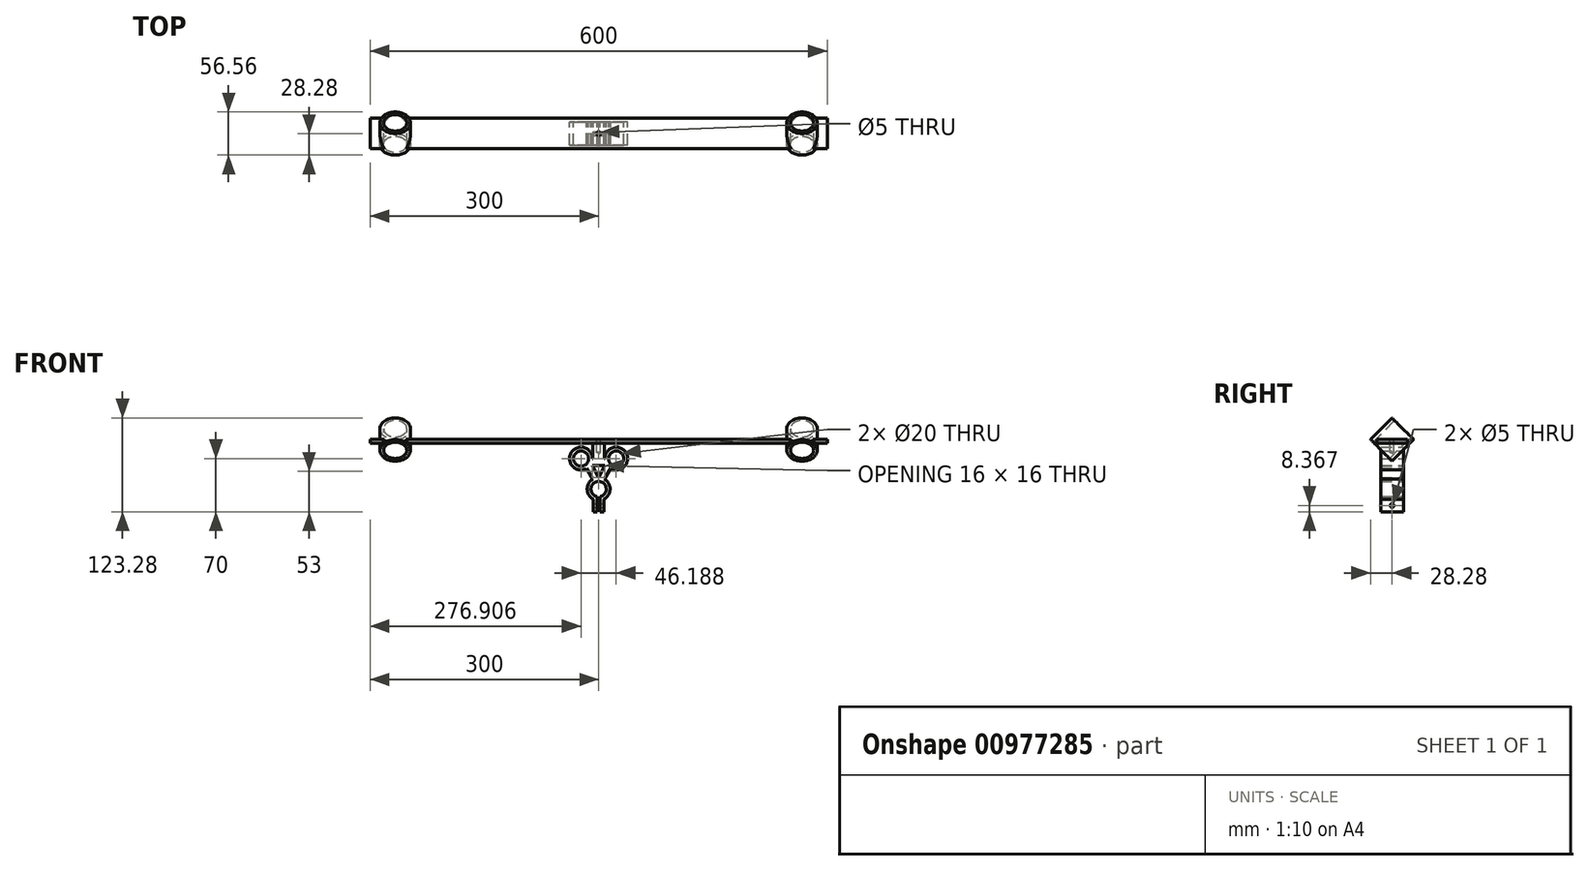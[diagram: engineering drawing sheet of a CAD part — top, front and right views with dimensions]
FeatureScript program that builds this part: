
annotation { "Feature Type Name" : "Feature", "Feature Type Description" : "" }
export const myFeature = defineFeature(function(context is Context, id is Id, definition is map)
    precondition{}
    {
        {
            var Q0;
            Q0=qCreatedBy(makeId("Front.planeOp"),FACE);
            var sketch = newSketch(context, id + "F0", { "sketchPlane" : qUnion([Q0])});
            skCircle(sketch, "E0", {"center": v(0, 0) * mm, "radius": 10 * mm});
            skCircle(sketch, "E1", {"center": v(23.1, 40) * mm, "radius": 10 * mm});
            skCircle(sketch, "E2", {"center": v(-23.1, 40) * mm, "radius": 10 * mm});
            skCircle(sketch, "E3", {"center": v(-23.1, 40) * mm, "radius": 15 * mm});
            skCircle(sketch, "E4", {"center": v(23.1, 40) * mm, "radius": 15 * mm});
            skCircle(sketch, "E5", {"center": v(0, 0) * mm, "radius": 15 * mm});
            skLineSegment(sketch, "E6", {"start": v(0, 0) * mm, "end": v(-23.1, 40) * mm});
            skLineSegment(sketch, "E7", {"start": v(23.1, 40) * mm, "end": v(0, 0) * mm});
            skLineSegment(sketch, "E8", {"start": v(-23.1, 40) * mm, "end": v(23.1, 40) * mm});
            skLineSegment(sketch, "E9.bottom", {"start": v(-2, 0) * mm, "end": v(2, 0) * mm});
            skLineSegment(sketch, "E9.top", {"start": v(-2, -30) * mm, "end": v(2, -30) * mm});
            skLineSegment(sketch, "E9.left", {"start": v(-2, 0) * mm, "end": v(-2, -30) * mm});
            skLineSegment(sketch, "E9.right", {"start": v(2, 0) * mm, "end": v(2, -30) * mm});
            skPoint(sketch, "E9.middle", {"position": v(0, -15) * mm});
            skLineSegment(sketch, "E10.bottom", {"start": v(7, -30) * mm, "end": v(-7, -30) * mm});
            skLineSegment(sketch, "E10.top", {"start": v(7, 0) * mm, "end": v(-7, 0) * mm});
            skLineSegment(sketch, "E10.left", {"start": v(7, -30) * mm, "end": v(7, 0) * mm});
            skLineSegment(sketch, "E10.right", {"start": v(-7, -30) * mm, "end": v(-7, 0) * mm});
            skLineSegment(sketch, "E11.bottom", {"start": v(-7.5, 60) * mm, "end": v(7.5, 60) * mm});
            skLineSegment(sketch, "E11.top", {"start": v(-7.5, 20) * mm, "end": v(7.5, 20) * mm});
            skLineSegment(sketch, "E11.left", {"start": v(-7.5, 60) * mm, "end": v(-7.5, 20) * mm});
            skLineSegment(sketch, "E11.right", {"start": v(7.5, 60) * mm, "end": v(7.5, 20) * mm});
            skPoint(sketch, "E11.middle", {"position": v(0, 40) * mm});
            skSolve(sketch);
        }
        {
            var Q0;
            {var subQ0=sQuery(id+"F0.wireOp",EDGE,"E7");var subQ1=sQuery(id+"F0.wireOp",EDGE,"E1");var subQ2=makeQuery(id+"F0.imprint","INTERSECT",VERTEX,{"derivedFrom":[subQ1,subQ0]});Q0=makeQuery(id+"F0.imprint","IMPRINT",FACE,{"disambiguationData":[TD([[makeQuery(id+"F0.imprint","IMPRINT",EDGE,{"disambiguationData":[TD([[subQ2,-1.0]])],"derivedFrom":subQ1}),-1.0]])]});}
            var Q1;
            {var subQ0=sQuery(id+"F0.wireOp",EDGE,"E6");var subQ1=sQuery(id+"F0.wireOp",EDGE,"E2");var subQ2=makeQuery(id+"F0.imprint","INTERSECT",VERTEX,{"derivedFrom":[subQ1,subQ0]});Q1=makeQuery(id+"F0.imprint","IMPRINT",FACE,{"disambiguationData":[TD([[makeQuery(id+"F0.imprint","IMPRINT",EDGE,{"disambiguationData":[TD([[subQ2,1.0]])],"derivedFrom":subQ1}),-1.0]])]});}
            var Q2;
            {var subQ0=sQuery(id+"F0.wireOp",EDGE,"E10.right");var subQ1=sQuery(id+"F0.wireOp",EDGE,"E5");var subQ2=makeQuery(id+"F0.imprint","INTERSECT",VERTEX,{"derivedFrom":[subQ1,subQ0]});Q2=makeQuery(id+"F0.imprint","IMPRINT",FACE,{"disambiguationData":[TD([[makeQuery(id+"F0.imprint","IMPRINT",EDGE,{"disambiguationData":[TD([[subQ2,-1.0]])],"derivedFrom":subQ1}),-1.0]])]});}
            var Q3;
            {var subQ0=sQuery(id+"F0.wireOp",EDGE,"E10.left");var subQ1=sQuery(id+"F0.wireOp",EDGE,"E5");var subQ2=makeQuery(id+"F0.imprint","INTERSECT",VERTEX,{"derivedFrom":[subQ1,subQ0]});Q3=makeQuery(id+"F0.imprint","IMPRINT",FACE,{"disambiguationData":[TD([[makeQuery(id+"F0.imprint","IMPRINT",EDGE,{"disambiguationData":[TD([[subQ2,1.0]])],"derivedFrom":subQ1}),-1.0]])]});}
            var Q4;
            {var subQ0=sQuery(id+"F0.wireOp",EDGE,"E6");var subQ1=sQuery(id+"F0.wireOp",EDGE,"E0");var subQ2=makeQuery(id+"F0.imprint","INTERSECT",VERTEX,{"derivedFrom":[subQ1,subQ0]});Q4=makeQuery(id+"F0.imprint","IMPRINT",FACE,{"disambiguationData":[TD([[makeQuery(id+"F0.imprint","IMPRINT",EDGE,{"disambiguationData":[TD([[subQ2,-1.0]])],"derivedFrom":subQ1}),-1.0]])]});}
            var Q5;
            {var subQ0=sQuery(id+"F0.wireOp",EDGE,"E7");var subQ1=sQuery(id+"F0.wireOp",EDGE,"E0");var subQ2=makeQuery(id+"F0.imprint","INTERSECT",VERTEX,{"derivedFrom":[subQ1,subQ0]});Q5=makeQuery(id+"F0.imprint","IMPRINT",FACE,{"disambiguationData":[TD([[makeQuery(id+"F0.imprint","IMPRINT",EDGE,{"disambiguationData":[TD([[subQ2,1.0]])],"derivedFrom":subQ1}),-1.0]])]});}
            var Q6;
            {var subQ0=sQuery(id+"F0.wireOp",EDGE,"E7");var subQ1=sQuery(id+"F0.wireOp",EDGE,"E1");var subQ2=makeQuery(id+"F0.imprint","INTERSECT",VERTEX,{"derivedFrom":[subQ1,subQ0]});Q6=makeQuery(id+"F0.imprint","IMPRINT",FACE,{"disambiguationData":[TD([[makeQuery(id+"F0.imprint","IMPRINT",EDGE,{"disambiguationData":[TD([[subQ2,1.0]])],"derivedFrom":subQ1}),-1.0]])]});}
            var Q7;
            {var subQ0=sQuery(id+"F0.wireOp",EDGE,"E6");var subQ1=sQuery(id+"F0.wireOp",EDGE,"E2");var subQ2=makeQuery(id+"F0.imprint","INTERSECT",VERTEX,{"derivedFrom":[subQ1,subQ0]});Q7=makeQuery(id+"F0.imprint","IMPRINT",FACE,{"disambiguationData":[TD([[makeQuery(id+"F0.imprint","IMPRINT",EDGE,{"disambiguationData":[TD([[subQ2,-1.0]])],"derivedFrom":subQ1}),-1.0]])]});}
            var Q8;
            {var subQ0=sQuery(id+"F0.wireOp",EDGE,"E6");var subQ5=sQuery(id+"F0.wireOp",EDGE,"E3");var subQ6=makeQuery(id+"F0.imprint","INTERSECT",VERTEX,{"derivedFrom":[subQ5,subQ0]});Q8=makeQuery(id+"F0.imprint","IMPRINT",FACE,{"disambiguationData":[TD([[makeQuery(id+"F0.imprint","IMPRINT",EDGE,{"disambiguationData":[TD([[subQ6,-1.0]])],"derivedFrom":subQ5}),-1.0]])]});}
            var Q9;
            {var subQ0=sQuery(id+"F0.wireOp",EDGE,"E6");var subQ1=sQuery(id+"F0.wireOp",EDGE,"E0");var subQ2=makeQuery(id+"F0.imprint","INTERSECT",VERTEX,{"derivedFrom":[subQ1,subQ0]});Q9=makeQuery(id+"F0.imprint","IMPRINT",FACE,{"disambiguationData":[TD([[makeQuery(id+"F0.imprint","IMPRINT",EDGE,{"disambiguationData":[TD([[subQ2,1.0]])],"derivedFrom":subQ1}),-1.0]])]});}
            var Q10;
            {var subQ0=sQuery(id+"F0.wireOp",EDGE,"E10.right");var subQ1=sQuery(id+"F0.wireOp",EDGE,"E0");var subQ2=makeQuery(id+"F0.imprint","INTERSECT",VERTEX,{"derivedFrom":[subQ1,subQ0]});Q10=makeQuery(id+"F0.imprint","IMPRINT",FACE,{"disambiguationData":[TD([[makeQuery(id+"F0.imprint","IMPRINT",EDGE,{"disambiguationData":[TD([[subQ2,-1.0]])],"derivedFrom":subQ1}),-1.0]])]});}
            var Q11;
            {var subQ0=sQuery(id+"F0.wireOp",EDGE,"E9.right");var subQ1=sQuery(id+"F0.wireOp",EDGE,"E0");var subQ2=makeQuery(id+"F0.imprint","INTERSECT",VERTEX,{"derivedFrom":[subQ1,subQ0]});Q11=makeQuery(id+"F0.imprint","IMPRINT",FACE,{"disambiguationData":[TD([[makeQuery(id+"F0.imprint","IMPRINT",EDGE,{"disambiguationData":[TD([[subQ2,-1.0]])],"derivedFrom":subQ1}),-1.0]])]});}
            var Q12;
            {var subQ5=sQuery(id+"F0.wireOp",EDGE,"E11.top");Q12=makeQuery(id+"F0.imprint","IMPRINT",FACE,{"disambiguationData":[TD([[makeQuery(id+"F0.imprint","IMPRINT",EDGE,{"derivedFrom":subQ5}),1.0]])]});}
            var Q13;
            {var subQ5=sQuery(id+"F0.wireOp",EDGE,"E11.bottom");Q13=makeQuery(id+"F0.imprint","IMPRINT",FACE,{"disambiguationData":[TD([[makeQuery(id+"F0.imprint","IMPRINT",EDGE,{"derivedFrom":subQ5}),-1.0]])]});}
            extrude(context, id + "F1", {"entities" : qUnion([Q0, Q1, Q2, Q3, Q4, Q5, Q6, Q7, Q8, Q9, Q10, Q11, Q12, Q13]), "depth" : 30 * mm, "offsetDistance" : 25 * mm});
        }
        {
            var Q0;
            Q0=makeQuery(id+"F1.opExtrude","SWEPT_FACE",FACE,{"disambiguationData":[OSD([sQuery(id+"F0.wireOp",EDGE,"E11.bottom")])]});
            var sketch = newSketch(context, id + "F2", { "sketchPlane" : qUnion([Q0])});
            skPoint(sketch, "E12", {"position": v(0, -15) * mm});
            skPoint(sketch, "E12.positionSnap0", {"position": v(-7.5, -15) * mm});
            skSolve(sketch);
        }
        {
            var Q0;
            Q0=sQuery(id+"F2.wireOp",VERTEX,"E12");
            var Q1;
            Q1=makeQuery(id+"F1.opExtrude","SWEPT_BODY",BODY,{"disambiguationData":[OSD([sQuery(id+"F0.wireOp",EDGE,"E0"),sQuery(id+"F0.wireOp",EDGE,"E1"),sQuery(id+"F0.wireOp",EDGE,"E2"),sQuery(id+"F0.wireOp",EDGE,"E3"),sQuery(id+"F0.wireOp",EDGE,"E4"),sQuery(id+"F0.wireOp",EDGE,"E5"),sQuery(id+"F0.wireOp",EDGE,"E6"),sQuery(id+"F0.wireOp",EDGE,"E7"),sQuery(id+"F0.wireOp",EDGE,"E8"),sQuery(id+"F0.wireOp",EDGE,"E9.left"),sQuery(id+"F0.wireOp",EDGE,"E9.right"),sQuery(id+"F0.wireOp",EDGE,"E10.bottom"),sQuery(id+"F0.wireOp",EDGE,"E10.left"),sQuery(id+"F0.wireOp",EDGE,"E10.right"),sQuery(id+"F0.wireOp",EDGE,"E11.bottom"),sQuery(id+"F0.wireOp",EDGE,"E11.left"),sQuery(id+"F0.wireOp",EDGE,"E11.right")])]});
            hole(context, id + "F3", {"style" : HoleStyle.SIMPLE, "endStyle" : HoleEndStyle.BLIND, "holeDiameter" : 5 * mm, "majorDiameter" : 5 * mm, "holeDepth" : 12 * mm, "isTappedThrough" : true, "tappedDepth" : 12 * mm, "tapClearance" : 3, "locations" : qUnion([Q0]), "scope" : qUnion([Q1])});
        }
        {
            var Q0;
            Q0=makeQuery(id+"F1.opExtrude","SWEPT_FACE",FACE,{"disambiguationData":[OSD([sQuery(id+"F0.wireOp",EDGE,"E10.left")])]});
            var sketch = newSketch(context, id + "F4", { "sketchPlane" : qUnion([Q0])});
            skPoint(sketch, "E13", {"position": v(-15, -21.63) * mm});
            skPoint(sketch, "E13.positionSnap0", {"position": v(0, -21.63) * mm});
            skPoint(sketch, "E13.positionSnap1", {"position": v(-15, -30) * mm});
            skCircle(sketch, "E14", {"center": v(-15, -21.63) * mm, "radius": 2.5 * mm});
            skSolve(sketch);
        }
        {
            var Q0;
            Q0=makeQuery(id+"F4.imprint","IMPRINT",FACE,{"disambiguationData":[TD([[makeQuery(id+"F4.imprint","IMPRINT",EDGE,{"derivedFrom":sQuery(id+"F4.wireOp",EDGE,"E14")}),1.0]])]});
            extrude(context, id + "F5", {"entities" : qUnion([Q0]), "operationType" : NewBodyOperationType.REMOVE, "oppositeDirection" : true, "depth" : 25 * mm, "offsetDistance" : 25 * mm});
        }
        {
            var Q0;
            Q0=makeQuery(id+"F1.opExtrude","SWEPT_FACE",FACE,{"disambiguationData":[OSD([sQuery(id+"F0.wireOp",EDGE,"E11.bottom")])]});
            var sketch = newSketch(context, id + "F6", { "sketchPlane" : qUnion([Q0])});
            skLineSegment(sketch, "E15.bottom", {"start": v(-300, 5) * mm, "end": v(300, 5) * mm});
            skLineSegment(sketch, "E15.top", {"start": v(-300, -35) * mm, "end": v(300, -35) * mm});
            skLineSegment(sketch, "E15.left", {"start": v(-300, 5) * mm, "end": v(-300, -35) * mm});
            skLineSegment(sketch, "E15.right", {"start": v(300, 5) * mm, "end": v(300, -35) * mm});
            skPoint(sketch, "E15.middle", {"position": v(0, -15) * mm});
            skSolve(sketch);
        }
        {
            var Q0;
            Q0=qSketchRegion(id+"F6",true);
            extrude(context, id + "F7", {"entities" : qUnion([Q0]), "operationType" : NewBodyOperationType.ADD, "depth" : 5 * mm, "offsetDistance" : 25 * mm});
        }
        {
            var Q0;
            Q0=qSketchRegion(id+"F6",true);
            extrude(context, id + "F8", {"entities" : qUnion([Q0]), "operationType" : NewBodyOperationType.ADD, "depth" : 5 * mm, "offsetDistance" : 25 * mm});
        }
        {
            var Q0;
            Q0=makeQuery(id+"F7.opExtrude","CAP_FACE",FACE,{"disambiguationData":[OSD([sQuery(id+"F6.wireOp",EDGE,"E15.bottom"),sQuery(id+"F6.wireOp",EDGE,"E15.top"),sQuery(id+"F6.wireOp",EDGE,"E15.left"),sQuery(id+"F6.wireOp",EDGE,"E15.right")])],"isStart":false});
            var sketch = newSketch(context, id + "F9", { "sketchPlane" : qUnion([Q0])});
            skLineSegment(sketch, "E16", {"start": v(-300, -15) * mm, "end": v(300, -15) * mm, "construction": true});
            skLineSegment(sketch, "E17", {"start": v(0, 0) * mm, "end": v(0, -35) * mm, "construction": true});
            skLineSegment(sketch, "E18", {"start": v(-267, 5) * mm, "end": v(-267, -35) * mm, "construction": true});
            skLineSegment(sketch, "E19", {"start": v(267, 5) * mm, "end": v(267, -35) * mm, "construction": true});
            skCircle(sketch, "E20", {"center": v(-267, -15) * mm, "radius": 12.7 * mm});
            skCircle(sketch, "E21", {"center": v(-267, -15) * mm, "radius": 15.24 * mm});
            skCircle(sketch, "E22", {"center": v(267, -15) * mm, "radius": 12.7 * mm});
            skCircle(sketch, "E23", {"center": v(267, -15) * mm, "radius": 15.24 * mm});
            skSolve(sketch);
        }
        {
            var Q0;
            Q0=makeQuery(id+"F9.imprint","IMPRINT",FACE,{"disambiguationData":[TD([[makeQuery(id+"F9.imprint","IMPRINT",EDGE,{"derivedFrom":sQuery(id+"F9.wireOp",EDGE,"E22")}),1.0]])]});
            var Q1;
            Q1=makeQuery(id+"F9.imprint","IMPRINT",FACE,{"disambiguationData":[TD([[makeQuery(id+"F9.imprint","IMPRINT",EDGE,{"derivedFrom":sQuery(id+"F9.wireOp",EDGE,"E20")}),1.0]])]});
            extrude(context, id + "F10", {"entities" : qUnion([Q0, Q1]), "operationType" : NewBodyOperationType.REMOVE, "endBound" : BoundingType.THROUGH_ALL, "oppositeDirection" : true, "depth" : 25 * mm, "offsetDistance" : 25 * mm});
        }
        {
            var Q0;
            Q0=qCreatedBy(makeId("Right.planeOp"),FACE);
            var sketch = newSketch(context, id + "F11", { "sketchPlane" : qUnion([Q0])});
            skLineSegment(sketch, "E24", {"start": v(-15, 65) * mm, "end": v(-35.3, 85.3) * mm});
            skLineSegment(sketch, "E25", {"start": v(-15, 65) * mm, "end": v(-53.1, 65) * mm});
            skSolve(sketch);
        }
        {
            var Q0;
            Q0=sQuery(id+"F11.wireOp",EDGE,"E24");
            cPlane(context, id + "F12", {"entities" : qUnion([Q0]), "cplaneType" : CPlaneType.LINE_ANGLE, "offset" : 25 * mm, "angle" : 0 * degree, "width" : 150 * mm, "height" : 150 * mm});
        }
        {
            var Q0;
            Q0=qCreatedBy(id+"F12.planeOp",FACE);
            var sketch = newSketch(context, id + "F13", { "sketchPlane" : qUnion([Q0])});
            skCircle(sketch, "E26", {"center": v(267, 56.57) * mm, "radius": 15.24 * mm});
            skCircle(sketch, "E27", {"center": v(267, 56.57) * mm, "radius": 20 * mm});
            skSolve(sketch);
        }
        {
            var Q0;
            Q0=qSketchRegion(id+"F13",true);
            extrude(context, id + "F14", {"entities" : qUnion([Q0]), "operationType" : NewBodyOperationType.ADD, "depth" : 40 * mm, "offsetDistance" : 25 * mm, "symmetric" : true});
        }
        {
            var Q0;
            Q0=makeQuery(id+"F13.imprint","IMPRINT",FACE,{"disambiguationData":[TD([[makeQuery(id+"F13.imprint","IMPRINT",EDGE,{"derivedFrom":sQuery(id+"F13.wireOp",EDGE,"E26")}),1.0]])]});
            extrude(context, id + "F15", {"entities" : qUnion([Q0]), "operationType" : NewBodyOperationType.REMOVE, "oppositeDirection" : true, "depth" : 40 * mm, "offsetDistance" : 25 * mm, "symmetric" : true});
        }
        {
            var Q0;
            Q0=qCreatedBy(id+"F12.planeOp",FACE);
            var sketch = newSketch(context, id + "F16", { "sketchPlane" : qUnion([Q0])});
            skCircle(sketch, "E28", {"center": v(-267, 56.57) * mm, "radius": 20 * mm});
            skCircle(sketch, "E29", {"center": v(-267, 56.57) * mm, "radius": 15.24 * mm});
            skSolve(sketch);
        }
        {
            var Q0;
            Q0=makeQuery(id+"F16.imprint","IMPRINT",FACE,{"disambiguationData":[TD([[makeQuery(id+"F16.imprint","IMPRINT",EDGE,{"derivedFrom":sQuery(id+"F16.wireOp",EDGE,"E28")}),1.0]])]});
            extrude(context, id + "F17", {"entities" : qUnion([Q0]), "operationType" : NewBodyOperationType.ADD, "depth" : 40 * mm, "offsetDistance" : 25 * mm, "symmetric" : true});
        }
        {
            var Q0;
            Q0=makeQuery(id+"F16.imprint","IMPRINT",FACE,{"disambiguationData":[TD([[makeQuery(id+"F16.imprint","IMPRINT",EDGE,{"derivedFrom":sQuery(id+"F16.wireOp",EDGE,"E29")}),1.0]])]});
            extrude(context, id + "F18", {"entities" : qUnion([Q0]), "operationType" : NewBodyOperationType.REMOVE, "endBound" : BoundingType.THROUGH_ALL, "depth" : 25 * mm, "offsetDistance" : 25 * mm, "hasSecondDirection" : true, "secondDirectionOppositeDirection" : true, "secondDirectionDepth" : 30 * mm});
        }
        {
            var Q0;
            Q0=makeQuery(id+"F9.imprint","IMPRINT",FACE,{"disambiguationData":[TD([[makeQuery(id+"F9.imprint","IMPRINT",EDGE,{"derivedFrom":sQuery(id+"F9.wireOp",EDGE,"E21")}),-1.0]])]});
            var sketch = newSketch(context, id + "F19", { "sketchPlane" : qUnion([Q0])});
            skCircle(sketch, "E30", {"center": v(0, -15) * mm, "radius": 2.5 * mm});
            skSolve(sketch);
        }
        {
            var Q0;
            Q0=qSketchRegion(id+"F19",true);
            extrude(context, id + "F20", {"entities" : qUnion([Q0]), "operationType" : NewBodyOperationType.REMOVE, "oppositeDirection" : true, "depth" : 5 * mm, "offsetDistance" : 25 * mm});
        }
        {
            var Q0;
            Q0=makeQuery(id+"F1.opExtrude","CAP_FACE",FACE,{"disambiguationData":[OSD([sQuery(id+"F0.wireOp",EDGE,"E0"),sQuery(id+"F0.wireOp",EDGE,"E1"),sQuery(id+"F0.wireOp",EDGE,"E2"),sQuery(id+"F0.wireOp",EDGE,"E3"),sQuery(id+"F0.wireOp",EDGE,"E4"),sQuery(id+"F0.wireOp",EDGE,"E5"),sQuery(id+"F0.wireOp",EDGE,"E6"),sQuery(id+"F0.wireOp",EDGE,"E7"),sQuery(id+"F0.wireOp",EDGE,"E8"),sQuery(id+"F0.wireOp",EDGE,"E9.left"),sQuery(id+"F0.wireOp",EDGE,"E9.right"),sQuery(id+"F0.wireOp",EDGE,"E10.bottom"),sQuery(id+"F0.wireOp",EDGE,"E10.left"),sQuery(id+"F0.wireOp",EDGE,"E10.right"),sQuery(id+"F0.wireOp",EDGE,"E11.bottom"),sQuery(id+"F0.wireOp",EDGE,"E11.left"),sQuery(id+"F0.wireOp",EDGE,"E11.right")])],"isStart":true});
            var sketch = newSketch(context, id + "F21", { "sketchPlane" : qUnion([Q0])});
            skLineSegment(sketch, "E31", {"start": v(0, 15) * mm, "end": v(8, 31) * mm});
            skLineSegment(sketch, "E32", {"start": v(8, 31) * mm, "end": v(-8, 31) * mm});
            skLineSegment(sketch, "E33", {"start": v(-8, 31) * mm, "end": v(0, 15) * mm});
            skSolve(sketch);
        }
        {
            var Q0;
            Q0=makeQuery(id+"F21.imprint","IMPRINT",FACE,{"disambiguationData":[TD([[makeQuery(id+"F21.imprint","IMPRINT",EDGE,{"derivedFrom":sQuery(id+"F21.wireOp",EDGE,"E31")}),1.0]])]});
            extrude(context, id + "F22", {"entities" : qUnion([Q0]), "operationType" : NewBodyOperationType.REMOVE, "oppositeDirection" : true, "depth" : 40 * mm, "offsetDistance" : 25 * mm});
        }
    });
